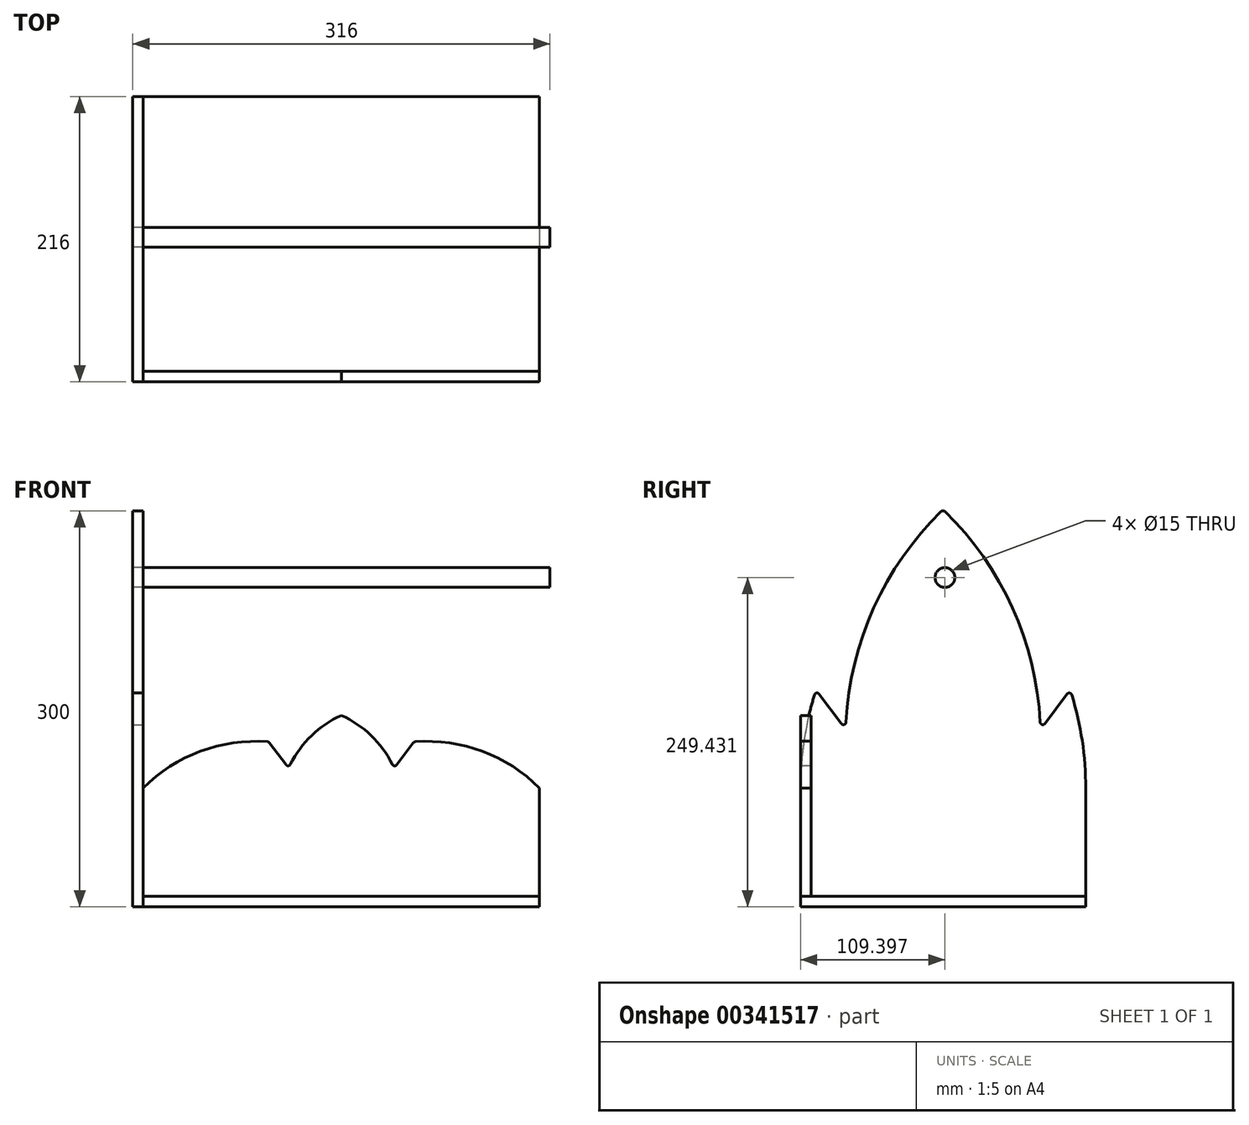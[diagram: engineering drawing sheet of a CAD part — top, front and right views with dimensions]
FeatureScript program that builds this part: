
annotation { "Feature Type Name" : "Feature", "Feature Type Description" : "" }
export const myFeature = defineFeature(function(context is Context, id is Id, definition is map)
    precondition{}
    {
        {
            assignVariable(context, id + "F0", {"name" : "d_flasche", "anyValue" : 90});
        }
        {
            assignVariable(context, id + "F1", {"name" : "dx_flasche", "anyValue" : 10});
        }
        {
            assignVariable(context, id + "F2", {"name" : "t_wand", "anyValue" : 8});
        }
        {
            var Q0;
            Q0=qCreatedBy(makeId("Top.planeOp"),FACE);
            var sketch = newSketch(context, id + "F3", { "sketchPlane" : qUnion([Q0])});
            skCircle(sketch, "E0", {"center": v(0, 50) * mm, "radius": 45 * mm, "construction": true});
            skCircle(sketch, "E1", {"center": v(0, -50) * mm, "radius": 45 * mm, "construction": true});
            skCircle(sketch, "E2", {"center": v(-100, 50) * mm, "radius": 45 * mm, "construction": true});
            skCircle(sketch, "E3", {"center": v(-100, -50) * mm, "radius": 45 * mm, "construction": true});
            skCircle(sketch, "E4.MirrorC", {"center": v(100, -50) * mm, "radius": 45 * mm, "construction": true});
            skCircle(sketch, "E5.MirrorC", {"center": v(100, 50) * mm, "radius": 45 * mm, "construction": true});
            skLineSegment(sketch, "E6", {"start": v(-100, 50) * mm, "end": v(-100, -50) * mm, "construction": true});
            skLineSegment(sketch, "E7", {"start": v(0, 50) * mm, "end": v(0, -50) * mm, "construction": true});
            skLineSegment(sketch, "E8", {"start": v(-100, 50) * mm, "end": v(0, 50) * mm, "construction": true});
            skLineSegment(sketch, "E9.bottom", {"start": v(-150, 108) * mm, "end": v(150, 108) * mm});
            skLineSegment(sketch, "E9.top", {"start": v(-150, -108) * mm, "end": v(150, -108) * mm});
            skLineSegment(sketch, "E9.left", {"start": v(-150, 108) * mm, "end": v(-150, -108) * mm});
            skLineSegment(sketch, "E9.right", {"start": v(150, 108) * mm, "end": v(150, -108) * mm});
            skLineSegment(sketch, "E10", {"start": v(-100, 50) * mm, "end": v(-145, 50) * mm, "construction": true});
            skLineSegment(sketch, "E11", {"start": v(-145, 50) * mm, "end": v(-150, 50) * mm, "construction": true});
            skLineSegment(sketch, "E12", {"start": v(-100, 50) * mm, "end": v(-100, 95) * mm, "construction": true});
            skLineSegment(sketch, "E13", {"start": v(-100, 95) * mm, "end": v(-100, 108) * mm, "construction": true});
            skSolve(sketch);
        }
        {
            var Q0;
            Q0 = qSketchRegion(id + "F3", true);
            extrude(context, id + "F4", {"entities" : qUnion([Q0]), "endBound" : BoundingType.SYMMETRIC, "depth" : (getVariable(context, 't_wand')) * mm});
        }
        {
            assignVariable(context, id + "F5", {"name" : "d_griff", "anyValue" : 15});
        }
        {
            var Q0;
            Q0=makeQuery(id+"F4.opExtrude","SWEPT_FACE",FACE,{"disambiguationData":[OSD([sQuery(id+"F3.wireOp",EDGE,"E9.left")])]});
            var sketch = newSketch(context, id + "F6", { "sketchPlane" : qUnion([Q0])});
            skLineSegment(sketch, "E14", {"start": v(108, -4) * mm, "end": v(-108, -4) * mm});
            skLineSegment(sketch, "E15", {"start": v(-108, -4) * mm, "end": v(-108, 86) * mm});
            skLineSegment(sketch, "E16", {"start": v(-93.87, 157.2) * mm, "end": v(-77.07, 134.8) * mm});
            skArc(sketch, "E17", {"start": v(-97.38, 156.59) * mm, "mid": v(-105.33, 121.7) * mm, "end": v(-108, 86) * mm});
            skArc(sketch, "E18", {"start": v(-1.4, 295.43) * mm, "mid": v(-52.5, 222.47) * mm, "end": v(-73.48, 135.9) * mm});
            skPoint(sketch, "E19.visualSharp", {"position": v(-96.2, 160.31) * mm});
            skArc(sketch, "E19.filletArc", {"start": v(-93.87, 157.2) * mm, "mid": v(-95.82, 157.97) * mm, "end": v(-97.38, 156.59) * mm});
            skPoint(sketch, "E20.visualSharp", {"position": v(-73.7, 130.3) * mm});
            skArc(sketch, "E20.filletArc", {"start": v(-77.07, 134.8) * mm, "mid": v(-74.89, 134.09) * mm, "end": v(-73.48, 135.9) * mm});
            skArc(sketch, "E21.MirrorCS", {"start": v(77.07, 134.8) * mm, "mid": v(74.89, 134.09) * mm, "end": v(73.48, 135.9) * mm});
            skArc(sketch, "E22.MirrorCS", {"start": v(93.87, 157.2) * mm, "mid": v(95.82, 157.97) * mm, "end": v(97.38, 156.59) * mm});
            skPoint(sketch, "E23.MirrorP", {"position": v(96.2, 160.31) * mm});
            skArc(sketch, "E24.MirrorCS", {"start": v(1.4, 295.43) * mm, "mid": v(52.5, 222.47) * mm, "end": v(73.48, 135.9) * mm});
            skLineSegment(sketch, "E25.MirrorCS", {"start": v(108, -4) * mm, "end": v(108, 86) * mm});
            skLineSegment(sketch, "E26.MirrorCS", {"start": v(-108, -4) * mm, "end": v(108, -4) * mm});
            skArc(sketch, "E27.MirrorCS", {"start": v(97.38, 156.59) * mm, "mid": v(105.33, 121.7) * mm, "end": v(108, 86) * mm});
            skPoint(sketch, "E28.MirrorP", {"position": v(73.7, 130.3) * mm});
            skLineSegment(sketch, "E29.MirrorCS", {"start": v(93.87, 157.2) * mm, "end": v(77.07, 134.8) * mm});
            skArc(sketch, "E30.filletArc", {"start": v(1.4, 295.43) * mm, "mid": v(0, 296) * mm, "end": v(-1.4, 295.43) * mm});
            skSolve(sketch);
        }
        {
            var Q0;
            Q0 = qSketchRegion(id + "F6", true);
            extrude(context, id + "F7", {"entities" : qUnion([Q0]), "depth" : (getVariable(context, 't_wand')) * mm});
        }
        {
            var Q0;
            Q0=makeQuery(id+"F7.opExtrude","CAP_FACE",FACE,{"disambiguationData":[OSD([sQuery(id+"F6.wireOp",EDGE,"E15"),sQuery(id+"F6.wireOp",EDGE,"E16"),sQuery(id+"F6.wireOp",EDGE,"E17"),sQuery(id+"F6.wireOp",EDGE,"E18"),sQuery(id+"F6.wireOp",EDGE,"E19.filletArc"),sQuery(id+"F6.wireOp",EDGE,"E20.filletArc"),sQuery(id+"F6.wireOp",EDGE,"E21.MirrorCS"),sQuery(id+"F6.wireOp",EDGE,"E22.MirrorCS"),sQuery(id+"F6.wireOp",EDGE,"E24.MirrorCS"),sQuery(id+"F6.wireOp",EDGE,"E25.MirrorCS"),sQuery(id+"F6.wireOp",EDGE,"E26.MirrorCS"),sQuery(id+"F6.wireOp",EDGE,"E27.MirrorCS"),sQuery(id+"F6.wireOp",EDGE,"E29.MirrorCS")])],"isStart":false});
            var sketch = newSketch(context, id + "F8", { "sketchPlane" : qUnion([Q0])});
            skLineSegment(sketch, "E31", {"start": v(-1.4, 295.43) * mm, "end": v(-1.4, 118.32) * mm, "construction": true});
            skPoint(sketch, "E32", {"position": v(-1.4, 245.43) * mm});
            skSolve(sketch);
        }
        {
            var Q0;
            Q0=sQuery(id+"F8.wireOp",VERTEX,"E32");
            var Q1;
            Q1=makeQuery(id+"F7.opExtrude","SWEPT_BODY",BODY,{"disambiguationData":[OSD([sQuery(id+"F6.wireOp",EDGE,"E15"),sQuery(id+"F6.wireOp",EDGE,"E16"),sQuery(id+"F6.wireOp",EDGE,"E17"),sQuery(id+"F6.wireOp",EDGE,"E18"),sQuery(id+"F6.wireOp",EDGE,"E19.filletArc"),sQuery(id+"F6.wireOp",EDGE,"E20.filletArc"),sQuery(id+"F6.wireOp",EDGE,"E21.MirrorCS"),sQuery(id+"F6.wireOp",EDGE,"E22.MirrorCS"),sQuery(id+"F6.wireOp",EDGE,"E24.MirrorCS"),sQuery(id+"F6.wireOp",EDGE,"E25.MirrorCS"),sQuery(id+"F6.wireOp",EDGE,"E26.MirrorCS"),sQuery(id+"F6.wireOp",EDGE,"E27.MirrorCS"),sQuery(id+"F6.wireOp",EDGE,"E29.MirrorCS")])]});
            hole(context, id + "F9", {"style" : HoleStyle.SIMPLE, "endStyle" : HoleEndStyle.THROUGH, "holeDiameter" : (getVariable(context, 'd_griff')) * mm, "isTappedThrough" : true, "tappedDepth" : 12 * mm, "tapClearance" : 3, "locations" : qUnion([Q0]), "scope" : qUnion([Q1])});
        }
        {
            var Q0;
            Q0=makeQuery(id+"F7.opExtrude","SWEPT_FACE",FACE,{"disambiguationData":[OSD([sQuery(id+"F6.wireOp",EDGE,"E25.MirrorCS")])]});
            var sketch = newSketch(context, id + "F10", { "sketchPlane" : qUnion([Q0])});
            skLineSegment(sketch, "E33", {"start": v(-150, 4) * mm, "end": v(0, 4) * mm});
            skLineSegment(sketch, "E34", {"start": v(-150, 4) * mm, "end": v(-150, 86) * mm});
            skLineSegment(sketch, "E35", {"start": v(-54.46, 120.28) * mm, "end": v(-41.98, 103.64) * mm});
            skArc(sketch, "E36", {"start": v(-55.9, 121.07) * mm, "mid": v(-106.8, 113.85) * mm, "end": v(-150, 86) * mm});
            skLineSegment(sketch, "E37", {"start": v(0, -4) * mm, "end": v(0, 196.45) * mm, "construction": true});
            skArc(sketch, "E38", {"start": v(0, 141) * mm, "mid": v(-22.49, 125.8) * mm, "end": v(-38.6, 103.95) * mm});
            skPoint(sketch, "E39.visualSharp", {"position": v(-55, 121) * mm});
            skArc(sketch, "E39.filletArc", {"start": v(-54.46, 120.28) * mm, "mid": v(-55.1, 120.83) * mm, "end": v(-55.9, 121.07) * mm});
            skPoint(sketch, "E40.visualSharp", {"position": v(-40, 101) * mm});
            skArc(sketch, "E40.filletArc", {"start": v(-41.98, 103.64) * mm, "mid": v(-40.2, 102.85) * mm, "end": v(-38.6, 103.95) * mm});
            skArc(sketch, "E41.MirrorCS", {"start": v(54.46, 120.28) * mm, "mid": v(55.1, 120.83) * mm, "end": v(55.9, 121.07) * mm});
            skArc(sketch, "E42.MirrorCS", {"start": v(41.98, 103.64) * mm, "mid": v(40.2, 102.85) * mm, "end": v(38.6, 103.95) * mm});
            skLineSegment(sketch, "E43.MirrorCS", {"start": v(150, 4) * mm, "end": v(0, 4) * mm});
            skArc(sketch, "E44.MirrorCS", {"start": v(0, 141) * mm, "mid": v(22.49, 125.8) * mm, "end": v(38.6, 103.95) * mm});
            skLineSegment(sketch, "E45.MirrorCS", {"start": v(150, 4) * mm, "end": v(150, 86) * mm});
            skLineSegment(sketch, "E46.MirrorCS", {"start": v(54.46, 120.28) * mm, "end": v(41.98, 103.64) * mm});
            skPoint(sketch, "E47.MirrorP", {"position": v(40, 101) * mm});
            skArc(sketch, "E48.MirrorCS", {"start": v(55.9, 121.07) * mm, "mid": v(106.8, 113.85) * mm, "end": v(150, 86) * mm});
            skPoint(sketch, "E49.MirrorP", {"position": v(55, 121) * mm});
            skSolve(sketch);
        }
        {
            var Q0;
            Q0 = qSketchRegion(id + "F10", true);
            extrude(context, id + "F11", {"entities" : qUnion([Q0]), "oppositeDirection" : true, "depth" : (getVariable(context, 't_wand')) * mm});
        }
        {
            var Q0;
            Q0=makeQuery(id+"F7.opExtrude","CAP_FACE",FACE,{"disambiguationData":[OSD([sQuery(id+"F6.wireOp",EDGE,"E15"),sQuery(id+"F6.wireOp",EDGE,"E16"),sQuery(id+"F6.wireOp",EDGE,"E17"),sQuery(id+"F6.wireOp",EDGE,"E18"),sQuery(id+"F6.wireOp",EDGE,"E19.filletArc"),sQuery(id+"F6.wireOp",EDGE,"E20.filletArc"),sQuery(id+"F6.wireOp",EDGE,"E21.MirrorCS"),sQuery(id+"F6.wireOp",EDGE,"E22.MirrorCS"),sQuery(id+"F6.wireOp",EDGE,"E24.MirrorCS"),sQuery(id+"F6.wireOp",EDGE,"E25.MirrorCS"),sQuery(id+"F6.wireOp",EDGE,"E26.MirrorCS"),sQuery(id+"F6.wireOp",EDGE,"E27.MirrorCS"),sQuery(id+"F6.wireOp",EDGE,"E29.MirrorCS")])],"isStart":false});
            var sketch = newSketch(context, id + "F12", { "sketchPlane" : qUnion([Q0])});
            skCircle(sketch, "E50", {"center": v(-1.4, 245.43) * mm, "radius": 7.5 * mm});
            skPoint(sketch, "E50.first.point", {"position": v(-3.82, 252.53) * mm});
            skPoint(sketch, "E50.second.point", {"position": v(-4.44, 238.57) * mm});
            skPoint(sketch, "E50.third.point", {"position": v(5.68, 242.94) * mm});
            skSolve(sketch);
        }
        {
            var Q0;
            Q0 = qSketchRegion(id + "F12", true);
            var Q1;
            Q1=makeQuery(id+"F11.opExtrude","CAP_VERTEX",VERTEX,{"disambiguationData":[OSD([sQuery(id+"F10.wireOp",EDGE,"c33fb3c8-dc49-4c38-8df6-f6b4586b52f10.MirrorCS"),sQuery(id+"F10.wireOp",EDGE,"c33fb3c8-dc49-4c38-8df6-f6b4586b52f12.MirrorCS")])],"isStart":true});
            extrude(context, id + "F13", {"entities" : qUnion([Q0]), "oppositeDirection" : true, "endBoundEntityVertex" : qUnion([Q1]), "depth" : (2 * getVariable(context, 't_wand') + 3 * getVariable(context, 'd_flasche') + 3 * getVariable(context, 'dx_flasche')) * mm});
        }
    });
